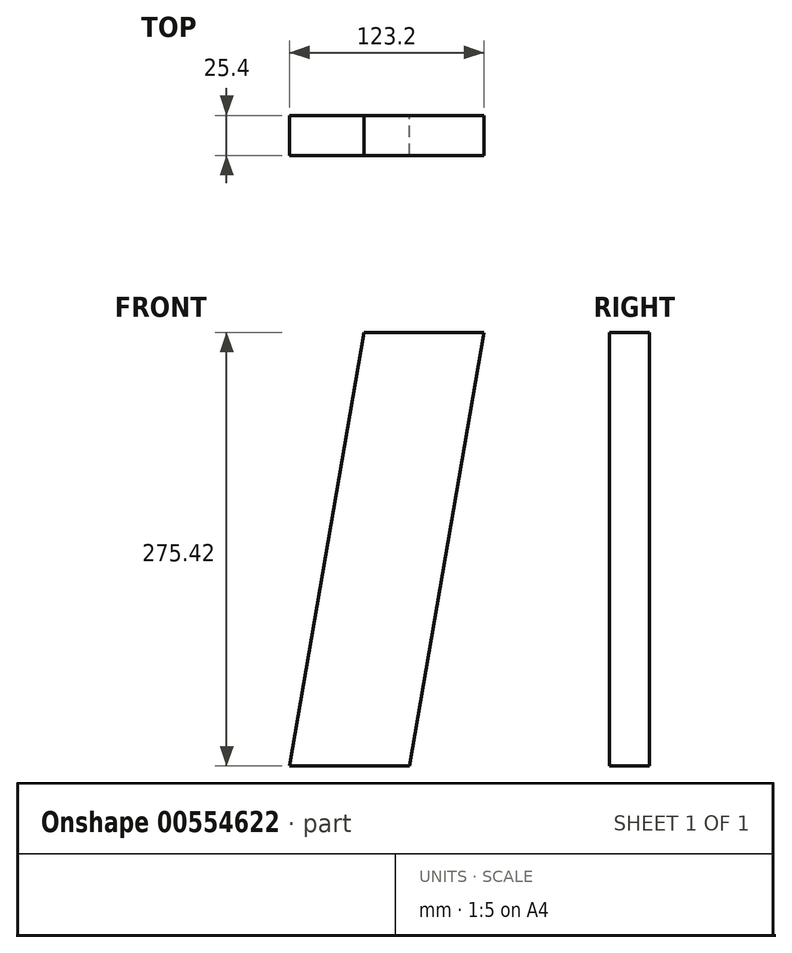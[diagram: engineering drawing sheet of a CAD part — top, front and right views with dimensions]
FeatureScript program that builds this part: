
annotation { "Feature Type Name" : "Feature", "Feature Type Description" : "" }
export const myFeature = defineFeature(function(context is Context, id is Id, definition is map)
    precondition{}
    {
        {
            var Q0;
            Q0=qCreatedBy(makeId("Front.planeOp"),FACE);
            var sketch = newSketch(context, id + "F0", { "sketchPlane" : qUnion([Q0])});
            skLineSegment(sketch, "E0", {"start": v(0, 66.2) * mm, "end": v(76.2, 66.2) * mm});
            skLineSegment(sketch, "E1", {"start": v(76.2, 66.2) * mm, "end": v(29.2, -209.23) * mm});
            skLineSegment(sketch, "E2", {"start": v(29.2, -209.23) * mm, "end": v(-47, -209.23) * mm});
            skLineSegment(sketch, "E3", {"start": v(-47, -209.23) * mm, "end": v(0, 66.2) * mm});
            skSolve(sketch);
        }
        {
            var Q0;
            Q0 = qSketchRegion(id + "F0", true);
            extrude(context, id + "F1", {"entities" : qUnion([Q0]), "depth" : 25.4 * mm, "offsetDistance" : 25.4 * mm});
        }
    });
